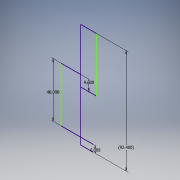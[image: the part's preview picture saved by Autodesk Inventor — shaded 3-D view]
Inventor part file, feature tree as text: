
AUTODESK INVENTOR PART (.ipt)
format: ipt  version: 2018 (Build 220112000, 112)  size: 92,160 bytes
history: native  units: in
note: dims shown in document units (in); Inventor stores cm internally (conversion verified against a paired STEP export)
features: sketch x1
ambient origin geometry x8: Origin, YZ Plane, XZ Plane, XY Plane, X Axis, Y Axis, Z Axis, Center Point
feature tree (1):
  sketch  "Sketch1"  dims[d0=48.0in d2=9.6in d5=6.0in d6=92.4in]
